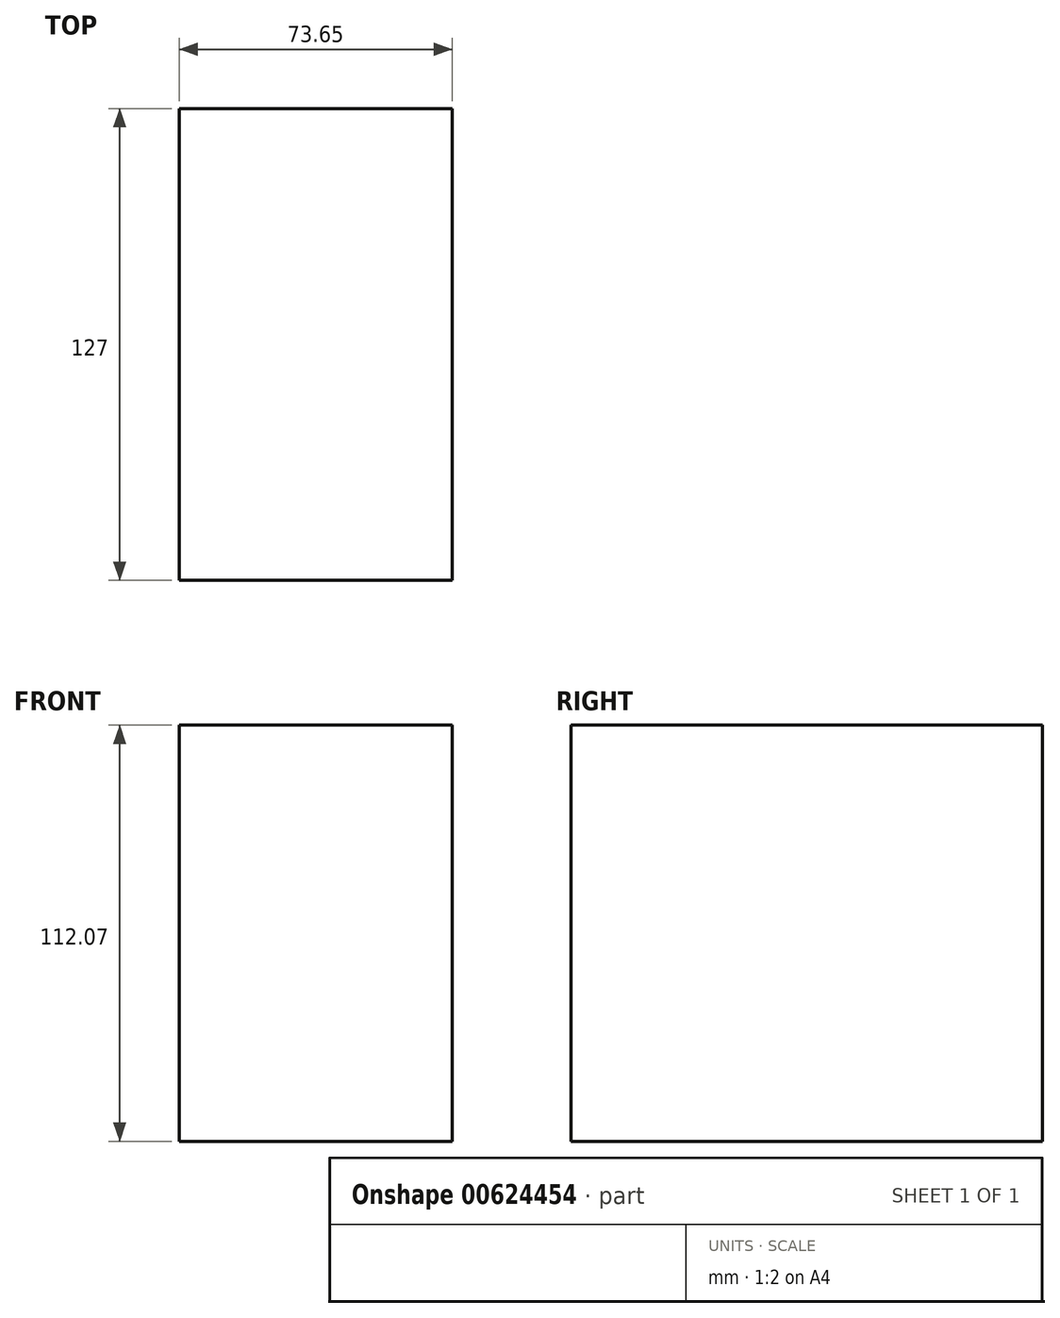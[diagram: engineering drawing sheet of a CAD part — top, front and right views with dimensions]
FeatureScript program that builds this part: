
annotation { "Feature Type Name" : "Feature", "Feature Type Description" : "" }
export const myFeature = defineFeature(function(context is Context, id is Id, definition is map)
    precondition{}
    {
        {
            var Q0;
            Q0=qCreatedBy(makeId("Front.planeOp"),FACE);
            var sketch = newSketch(context, id + "F0", { "sketchPlane" : qUnion([Q0])});
            skLineSegment(sketch, "E0.bottom", {"start": v(-48.45, 56.1) * mm, "end": v(25.2, 56.1) * mm});
            skLineSegment(sketch, "E0.top", {"start": v(-48.45, -55.96) * mm, "end": v(25.2, -55.96) * mm});
            skLineSegment(sketch, "E0.left", {"start": v(-48.45, 56.1) * mm, "end": v(-48.45, -55.96) * mm});
            skLineSegment(sketch, "E0.right", {"start": v(25.2, 56.1) * mm, "end": v(25.2, -55.96) * mm});
            skSolve(sketch);
        }
        {
            var Q0;
            Q0=makeQuery(id+"F0.imprint","IMPRINT",FACE,{"disambiguationData":[TD([[makeQuery(id+"F0.imprint","IMPRINT",EDGE,{"derivedFrom":sQuery(id+"F0.wireOp",EDGE,"E0.bottom")}),-1.0]])]});
            extrude(context, id + "F1", {"entities" : qUnion([Q0]), "depth" : 127 * mm, "offsetDistance" : 25.4 * mm});
        }
    });
